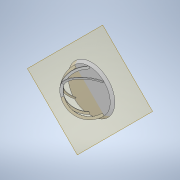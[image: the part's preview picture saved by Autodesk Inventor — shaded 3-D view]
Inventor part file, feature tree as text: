
AUTODESK INVENTOR PART (.ipt)
format: ipt  version: 2021 (Build 250183000, 183)  size: 186,880 bytes
history: native  units: mm
features: sketch x3, other x2, revolve x1, extrude x1, pattern_circular x1
ambient origin geometry x8: Origin, YZ Plane, XZ Plane, XY Plane, X Axis, Y Axis, Z Axis, Center Point
bodies: Body1 (feature_tree)
feature tree (8):
  other  "ソリッド1"
  revolve  "回転1"
  sketch  "スケッチ2"
  other  "作業平面1"
  extrude  "押し出し1"  Depth=5000.0mm
  pattern_circular  "円形状パターン1"  Count=50  [1 undecoded]
  sketch  "スケッチ1"
  sketch  "スケッチ3"
note: 1 required parameter value undecoded (feature->parameter linkage not recoverable at this tier; creation-order binding heuristic only, values carry confidence <= 0.55)
